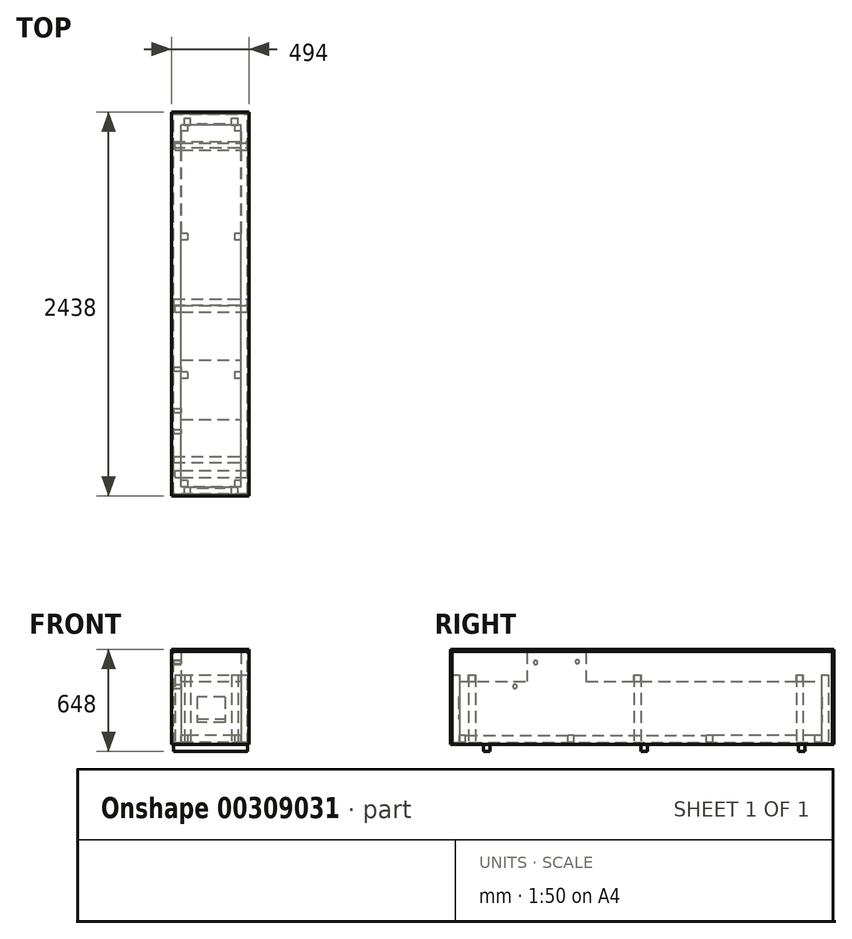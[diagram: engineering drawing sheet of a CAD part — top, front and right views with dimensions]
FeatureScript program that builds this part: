
annotation { "Feature Type Name" : "Feature", "Feature Type Description" : "" }
export const myFeature = defineFeature(function(context is Context, id is Id, definition is map)
    precondition{}
    {
        {
            var Q0;
            Q0=qCreatedBy(makeId("Right.planeOp"),FACE);
            var sketch = newSketch(context, id + "F0", { "sketchPlane" : qUnion([Q0])});
            skLineSegment(sketch, "E0.bottom", {"start": v(-1150, 195) * mm, "end": v(1150, 195) * mm});
            skLineSegment(sketch, "E0.top", {"start": v(-1150, -195) * mm, "end": v(-1110, -195) * mm});
            skLineSegment(sketch, "E0.left", {"start": v(-1150, 195) * mm, "end": v(-1150, -195) * mm});
            skLineSegment(sketch, "E0.right", {"start": v(1150, 195) * mm, "end": v(1150, -195) * mm});
            skPoint(sketch, "E0.middle", {"position": v(0, 0) * mm});
            skLineSegment(sketch, "E1.top", {"start": v(-1110, -148) * mm, "end": v(-460, -148) * mm});
            skLineSegment(sketch, "E1.left", {"start": v(-1110, -195) * mm, "end": v(-1110, -148) * mm});
            skLineSegment(sketch, "E1.right", {"start": v(-460, -195) * mm, "end": v(-460, -148) * mm});
            skLineSegment(sketch, "E2.top", {"start": v(1110, -148) * mm, "end": v(460, -148) * mm});
            skLineSegment(sketch, "E2.left", {"start": v(1110, -195) * mm, "end": v(1110, -148) * mm});
            skLineSegment(sketch, "E2.right", {"start": v(460, -195) * mm, "end": v(460, -148) * mm});
            skLineSegment(sketch, "E3.top", {"start": v(-420, -148) * mm, "end": v(420, -148) * mm});
            skLineSegment(sketch, "E3.left", {"start": v(-420, -195) * mm, "end": v(-420, -148) * mm});
            skLineSegment(sketch, "E3.right", {"start": v(420, -195) * mm, "end": v(420, -148) * mm});
            skLineSegment(sketch, "E4.trimOffspring", {"start": v(-460, -195) * mm, "end": v(-420, -195) * mm});
            skLineSegment(sketch, "E5.trimOffspring", {"start": v(420, -195) * mm, "end": v(460, -195) * mm});
            skLineSegment(sketch, "E6.trimOffspring", {"start": v(1110, -195) * mm, "end": v(1150, -195) * mm});
            skSolve(sketch);
        }
        {
            var Q0;
            Q0 = qSketchRegion(id + "F0", true);
            extrude(context, id + "F1", {"entities" : qUnion([Q0]), "depth" : 380 * mm});
        }
        {
            var Q0;
            Q0=makeQuery(id+"F1.opExtrude","SWEPT_FACE",FACE,{"disambiguationData":[OSD([sQuery(id+"F0.wireOp",EDGE,"E0.left")])]});
            var sketch = newSketch(context, id + "F2", { "sketchPlane" : qUnion([Q0])});
            skLineSegment(sketch, "E7.bottom", {"start": v(40, -195) * mm, "end": v(340, -195) * mm});
            skLineSegment(sketch, "E7.top", {"start": v(40, -148) * mm, "end": v(340, -148) * mm});
            skLineSegment(sketch, "E7.left", {"start": v(40, -195) * mm, "end": v(40, -148) * mm});
            skLineSegment(sketch, "E7.right", {"start": v(340, -195) * mm, "end": v(340, -148) * mm});
            skSolve(sketch);
        }
        {
            var Q0;
            Q0 = qSketchRegion(id + "F2", true);
            extrude(context, id + "F3", {"entities" : qUnion([Q0]), "operationType" : NewBodyOperationType.REMOVE, "endBound" : BoundingType.THROUGH_ALL, "oppositeDirection" : true, "depth" : 25 * mm});
        }
        {
            var Q0;
            Q0=makeQuery(id+"F1.opExtrude","SWEPT_FACE",FACE,{"disambiguationData":[OSD([sQuery(id+"F0.wireOp",EDGE,"E0.bottom")])]});
            var sketch = newSketch(context, id + "F4", { "sketchPlane" : qUnion([Q0])});
            skLineSegment(sketch, "E8.bottom", {"start": v(0, -720) * mm, "end": v(380, -720) * mm});
            skLineSegment(sketch, "E8.top", {"start": v(0, -345) * mm, "end": v(380, -345) * mm});
            skLineSegment(sketch, "E8.left", {"start": v(0, -720) * mm, "end": v(0, -345) * mm});
            skLineSegment(sketch, "E8.right", {"start": v(380, -720) * mm, "end": v(380, -345) * mm});
            skSolve(sketch);
        }
        {
            var Q0;
            Q0 = qSketchRegion(id + "F4", true);
            extrude(context, id + "F5", {"entities" : qUnion([Q0]), "operationType" : NewBodyOperationType.ADD, "depth" : 185 * mm});
        }
        {
            var Q0;
            Q0=makeQuery(id+"F1.opExtrude","SWEPT_FACE",FACE,{"disambiguationData":[OSD([sQuery(id+"F0.wireOp",EDGE,"E0.left")])]});
            var sketch = newSketch(context, id + "F6", { "sketchPlane" : qUnion([Q0])});
            skLineSegment(sketch, "E9.bottom", {"start": v(100, 95) * mm, "end": v(280, 95) * mm});
            skLineSegment(sketch, "E9.top", {"start": v(100, -45) * mm, "end": v(280, -45) * mm});
            skLineSegment(sketch, "E9.left", {"start": v(100, 95) * mm, "end": v(100, -45) * mm});
            skLineSegment(sketch, "E9.right", {"start": v(280, 95) * mm, "end": v(280, -45) * mm});
            skSolve(sketch);
        }
        {
            var Q0;
            Q0 = qSketchRegion(id + "F6", true);
            extrude(context, id + "F7", {"entities" : qUnion([Q0]), "operationType" : NewBodyOperationType.ADD, "depth" : 5 * mm});
        }
        {
            var Q0;
            Q0=makeQuery(id+"F1.opExtrude","SWEPT_FACE",FACE,{"disambiguationData":[OSD([sQuery(id+"F0.wireOp",EDGE,"E0.right")])]});
            var sketch = newSketch(context, id + "F8", { "sketchPlane" : qUnion([Q0])});
            skLineSegment(sketch, "E10.bottom", {"start": v(-280, 95) * mm, "end": v(-100, 95) * mm});
            skLineSegment(sketch, "E10.top", {"start": v(-280, -65) * mm, "end": v(-100, -65) * mm});
            skLineSegment(sketch, "E10.left", {"start": v(-280, 95) * mm, "end": v(-280, -65) * mm});
            skLineSegment(sketch, "E10.right", {"start": v(-100, 95) * mm, "end": v(-100, -65) * mm});
            skSolve(sketch);
        }
        {
            var Q0;
            Q0 = qSketchRegion(id + "F8", true);
            extrude(context, id + "F9", {"entities" : qUnion([Q0]), "operationType" : NewBodyOperationType.ADD, "depth" : 5 * mm});
        }
        {
            var Q0;
            Q0=makeQuery(id+"F5.boolean.opBoolean","MERGE",FACE,{"derivedFrom":[makeQuery(id+"F1.opExtrude","CAP_FACE",FACE,{"disambiguationData":[OSD([sQuery(id+"F0.wireOp",EDGE,"E0.bottom"),sQuery(id+"F0.wireOp",EDGE,"E0.top"),sQuery(id+"F0.wireOp",EDGE,"E0.left"),sQuery(id+"F0.wireOp",EDGE,"E0.right"),sQuery(id+"F0.wireOp",EDGE,"E1.top"),sQuery(id+"F0.wireOp",EDGE,"E1.left"),sQuery(id+"F0.wireOp",EDGE,"E1.right"),sQuery(id+"F0.wireOp",EDGE,"E2.top"),sQuery(id+"F0.wireOp",EDGE,"E2.left"),sQuery(id+"F0.wireOp",EDGE,"E2.right"),sQuery(id+"F0.wireOp",EDGE,"E3.top"),sQuery(id+"F0.wireOp",EDGE,"E3.left"),sQuery(id+"F0.wireOp",EDGE,"E3.right"),sQuery(id+"F0.wireOp",EDGE,"E4.trimOffspring"),sQuery(id+"F0.wireOp",EDGE,"E5.trimOffspring"),sQuery(id+"F0.wireOp",EDGE,"E6.trimOffspring")])],"isStart":true}),makeQuery(id+"F5.opExtrude","SWEPT_FACE",FACE,{"disambiguationData":[OSD([sQuery(id+"F4.wireOp",EDGE,"E8.left")])]})]});
            var sketch = newSketch(context, id + "F10", { "sketchPlane" : qUnion([Q0])});
            skCircle(sketch, "E11", {"center": v(399.4, 319.26) * mm, "radius": 12.5 * mm});
            skCircle(sketch, "E12", {"center": v(664.97, 313.36) * mm, "radius": 12.5 * mm});
            skCircle(sketch, "E13", {"center": v(796.28, 162.13) * mm, "radius": 12.5 * mm});
            skSolve(sketch);
        }
        {
            var Q0;
            Q0 = qSketchRegion(id + "F10", true);
            extrude(context, id + "F11", {"entities" : qUnion([Q0]), "operationType" : NewBodyOperationType.ADD, "depth" : 50 * mm});
        }
        {
            var Q0;
            {var subQ2=sQuery(id+"F0.wireOp",EDGE,"E0.top");Q0=makeQuery(id+"F3.boolean.opBoolean","SPLIT",FACE,{"disambiguationData":[TD([makeQuery(id+"F3.opExtrude","SWEPT_FACE",FACE,{"disambiguationData":[OSD([sQuery(id+"F2.wireOp",EDGE,"E7.right")])]})])],"derivedFrom":makeQuery(id+"F1.opExtrude","SWEPT_FACE",FACE,{"disambiguationData":[OSD([subQ2])]})});}
            var sketch = newSketch(context, id + "F12", { "sketchPlane" : qUnion([Q0])});
            skLineSegment(sketch, "E14.bottom", {"start": v(420, 1195) * mm, "end": v(-50, 1195) * mm});
            skLineSegment(sketch, "E14.top", {"start": v(420, -1219) * mm, "end": v(-50, -1219) * mm});
            skLineSegment(sketch, "E14.left", {"start": v(420, 1195) * mm, "end": v(420, -1219) * mm});
            skLineSegment(sketch, "E14.right", {"start": v(-50, 1195) * mm, "end": v(-50, -1219) * mm});
            skSolve(sketch);
        }
        {
            var Q0;
            Q0 = qSketchRegion(id + "F12", true);
            extrude(context, id + "F13", {"entities" : qUnion([Q0]), "depth" : 12 * mm});
        }
        {
            var Q0;
            Q0=makeQuery(id+"F13.opExtrude","SWEPT_FACE",FACE,{"disambiguationData":[OSD([sQuery(id+"F12.wireOp",EDGE,"E14.left")])]});
            var sketch = newSketch(context, id + "F14", { "sketchPlane" : qUnion([Q0])});
            skLineSegment(sketch, "E15.top", {"start": v(-1195, 385) * mm, "end": v(1219, 385) * mm});
            skLineSegment(sketch, "E15.left", {"start": v(-1195, -195) * mm, "end": v(-1195, 385) * mm});
            skLineSegment(sketch, "E15.right", {"start": v(1219, -195) * mm, "end": v(1219, 385) * mm});
            skLineSegment(sketch, "E16.top", {"start": v(-1195, -207) * mm, "end": v(1219, -207) * mm});
            skLineSegment(sketch, "E16.left", {"start": v(-1195, -195) * mm, "end": v(-1195, -207) * mm});
            skLineSegment(sketch, "E16.right", {"start": v(1219, -195) * mm, "end": v(1219, -207) * mm});
            skSolve(sketch);
        }
        {
            var Q0;
            Q0 = qSketchRegion(id + "F14", true);
            extrude(context, id + "F15", {"entities" : qUnion([Q0]), "depth" : 12 * mm});
        }
        {
            var Q0;
            Q0=makeQuery(id+"F15.opExtrude","SWEPT_BODY",BODY,{"disambiguationData":[OSD([sQuery(id+"F14.wireOp",EDGE,"E15.bottom"),sQuery(id+"F14.wireOp",EDGE,"E15.top"),sQuery(id+"F14.wireOp",EDGE,"E15.left"),sQuery(id+"F14.wireOp",EDGE,"E15.right")])]});
            transform(context, id + "F16", {"entities" : qUnion([Q0]), "transformType" : TransformType.TRANSLATION_3D, "dx" : -482 * mm, "dy" : 0 * mm, "dz" : 0 * mm, "makeCopy" : true});
        }
        {
            var Q0;
            Q0=makeQuery(id+"F13.opExtrude","CAP_FACE",FACE,{"disambiguationData":[OSD([sQuery(id+"F12.wireOp",EDGE,"E14.bottom"),sQuery(id+"F12.wireOp",EDGE,"E14.top"),sQuery(id+"F12.wireOp",EDGE,"E14.left"),sQuery(id+"F12.wireOp",EDGE,"E14.right")])],"isStart":true});
            var sketch = newSketch(context, id + "F17", { "sketchPlane" : qUnion([Q0])});
            skLineSegment(sketch, "E17.bottom", {"start": v(380, -1090) * mm, "end": v(420, -1090) * mm});
            skLineSegment(sketch, "E17.top", {"start": v(380, -1046) * mm, "end": v(420, -1046) * mm});
            skLineSegment(sketch, "E17.left", {"start": v(380, -1090) * mm, "end": v(380, -1046) * mm});
            skLineSegment(sketch, "E17.right", {"start": v(420, -1090) * mm, "end": v(420, -1046) * mm});
            skSolve(sketch);
        }
        {
            var Q0;
            Q0 = qSketchRegion(id + "F17", true);
            extrude(context, id + "F18", {"entities" : qUnion([Q0]), "depth" : 430 * mm});
        }
        {
            var Q0;
            Q0=makeQuery(id+"F13.opExtrude","SWEPT_FACE",FACE,{"disambiguationData":[OSD([sQuery(id+"F12.wireOp",EDGE,"E14.left")])]});
            var sketch = newSketch(context, id + "F19", { "sketchPlane" : qUnion([Q0])});
            skLineSegment(sketch, "E18.bottom", {"start": v(-995, -207) * mm, "end": v(-955, -207) * mm});
            skLineSegment(sketch, "E18.top", {"start": v(-995, -251) * mm, "end": v(-955, -251) * mm});
            skLineSegment(sketch, "E18.left", {"start": v(-995, -207) * mm, "end": v(-995, -251) * mm});
            skLineSegment(sketch, "E18.right", {"start": v(-955, -207) * mm, "end": v(-955, -251) * mm});
            skLineSegment(sketch, "E19.1.0.0", {"start": v(5, -207) * mm, "end": v(5, -251) * mm});
            skLineSegment(sketch, "E19.1.0.1", {"start": v(45, -207) * mm, "end": v(45, -251) * mm});
            skLineSegment(sketch, "E19.1.0.2", {"start": v(5, -207) * mm, "end": v(45, -207) * mm});
            skLineSegment(sketch, "E19.1.0.3", {"start": v(5, -251) * mm, "end": v(45, -251) * mm});
            skLineSegment(sketch, "E19.2.0.0", {"start": v(1005, -207) * mm, "end": v(1005, -251) * mm});
            skLineSegment(sketch, "E19.2.0.1", {"start": v(1045, -207) * mm, "end": v(1045, -251) * mm});
            skLineSegment(sketch, "E19.2.0.2", {"start": v(1005, -207) * mm, "end": v(1045, -207) * mm});
            skLineSegment(sketch, "E19.2.0.3", {"start": v(1005, -251) * mm, "end": v(1045, -251) * mm});
            skLineSegment(sketch, "E19.direction1", {"start": v(-995, -251) * mm, "end": v(5, -251) * mm, "construction": true});
            skSolve(sketch);
        }
        {
            var Q0;
            Q0 = qSketchRegion(id + "F19", true);
            var Q1;
            Q1=makeQuery(id+"F16.opPattern","COPY",FACE,{"derivedFrom":makeQuery(id+"F15.opExtrude","CAP_FACE",FACE,{"disambiguationData":[OSD([sQuery(id+"F14.wireOp",EDGE,"E15.bottom"),sQuery(id+"F14.wireOp",EDGE,"E15.top"),sQuery(id+"F14.wireOp",EDGE,"E15.left"),sQuery(id+"F14.wireOp",EDGE,"E15.right")])],"isStart":false}),"instanceName":"1"});
            extrude(context, id + "F20", {"entities" : qUnion([Q0]), "endBound" : BoundingType.UP_TO_SURFACE, "oppositeDirection" : true, "endBoundEntityFace" : qUnion([Q1]), "depth" : 25 * mm});
        }
        {
            var Q0;
            Q0=makeQuery(id+"F18.opExtrude","SWEPT_BODY",BODY,{"disambiguationData":[OSD([sQuery(id+"F17.wireOp",EDGE,"E17.bottom"),sQuery(id+"F17.wireOp",EDGE,"E17.top"),sQuery(id+"F17.wireOp",EDGE,"E17.left"),sQuery(id+"F17.wireOp",EDGE,"E17.right")])]});
            transform(context, id + "F21", {"entities" : qUnion([Q0]), "transformType" : TransformType.TRANSLATION_3D, "dx" : -420 * mm, "dy" : 0 * mm, "dz" : 0 * mm, "makeCopy" : true});
        }
        {
            var Q0;
            Q0=makeQuery(id+"F21.opPattern","COPY",FACE,{"derivedFrom":makeQuery(id+"F18.opExtrude","CAP_FACE",FACE,{"disambiguationData":[OSD([sQuery(id+"F17.wireOp",EDGE,"E17.bottom"),sQuery(id+"F17.wireOp",EDGE,"E17.top"),sQuery(id+"F17.wireOp",EDGE,"E17.left"),sQuery(id+"F17.wireOp",EDGE,"E17.right")])],"isStart":false}),"instanceName":"1"});
            var sketch = newSketch(context, id + "F22", { "sketchPlane" : qUnion([Q0])});
            skLineSegment(sketch, "E20.bottom", {"start": v(0, -1090) * mm, "end": v(380, -1090) * mm});
            skLineSegment(sketch, "E20.top", {"start": v(0, -1046) * mm, "end": v(380, -1046) * mm});
            skLineSegment(sketch, "E20.left", {"start": v(0, -1090) * mm, "end": v(0, -1046) * mm});
            skLineSegment(sketch, "E20.right", {"start": v(380, -1090) * mm, "end": v(380, -1046) * mm});
            skSolve(sketch);
        }
        {
            var Q0;
            Q0 = qSketchRegion(id + "F22", true);
            extrude(context, id + "F23", {"entities" : qUnion([Q0]), "oppositeDirection" : true, "depth" : 40 * mm});
        }
        {
            var Q0;
            Q0=makeQuery(id+"F23.opExtrude","SWEPT_BODY",BODY,{"disambiguationData":[OSD([sQuery(id+"F22.wireOp",EDGE,"E20.bottom"),sQuery(id+"F22.wireOp",EDGE,"E20.top"),sQuery(id+"F22.wireOp",EDGE,"E20.left"),sQuery(id+"F22.wireOp",EDGE,"E20.right")])]});
            var Q1;
            Q1=makeQuery(id+"F21.opPattern","COPY",BODY,{"derivedFrom":makeQuery(id+"F18.opExtrude","SWEPT_BODY",BODY,{"disambiguationData":[OSD([sQuery(id+"F17.wireOp",EDGE,"E17.bottom"),sQuery(id+"F17.wireOp",EDGE,"E17.top"),sQuery(id+"F17.wireOp",EDGE,"E17.left"),sQuery(id+"F17.wireOp",EDGE,"E17.right")])]}),"instanceName":"1"});
            var Q2;
            Q2=makeQuery(id+"F18.opExtrude","SWEPT_BODY",BODY,{"disambiguationData":[OSD([sQuery(id+"F17.wireOp",EDGE,"E17.bottom"),sQuery(id+"F17.wireOp",EDGE,"E17.top"),sQuery(id+"F17.wireOp",EDGE,"E17.left"),sQuery(id+"F17.wireOp",EDGE,"E17.right")])]});
            transform(context, id + "F24", {"entities" : qUnion([Q0, Q1, Q2]), "transformType" : TransformType.TRANSLATION_3D, "dx" : 0 * mm, "dy" : 1050 * mm, "dz" : 0 * mm, "makeCopy" : true});
        }
        {
            var Q0;
            Q0=makeQuery(id+"F23.opExtrude","SWEPT_BODY",BODY,{"disambiguationData":[OSD([sQuery(id+"F22.wireOp",EDGE,"E20.bottom"),sQuery(id+"F22.wireOp",EDGE,"E20.top"),sQuery(id+"F22.wireOp",EDGE,"E20.left"),sQuery(id+"F22.wireOp",EDGE,"E20.right")])]});
            var Q1;
            Q1=makeQuery(id+"F21.opPattern","COPY",BODY,{"derivedFrom":makeQuery(id+"F18.opExtrude","SWEPT_BODY",BODY,{"disambiguationData":[OSD([sQuery(id+"F17.wireOp",EDGE,"E17.bottom"),sQuery(id+"F17.wireOp",EDGE,"E17.top"),sQuery(id+"F17.wireOp",EDGE,"E17.left"),sQuery(id+"F17.wireOp",EDGE,"E17.right")])]}),"instanceName":"1"});
            var Q2;
            Q2=makeQuery(id+"F18.opExtrude","SWEPT_BODY",BODY,{"disambiguationData":[OSD([sQuery(id+"F17.wireOp",EDGE,"E17.bottom"),sQuery(id+"F17.wireOp",EDGE,"E17.top"),sQuery(id+"F17.wireOp",EDGE,"E17.left"),sQuery(id+"F17.wireOp",EDGE,"E17.right")])]});
            transform(context, id + "F25", {"entities" : qUnion([Q0, Q1, Q2]), "transformType" : TransformType.TRANSLATION_3D, "dx" : 0 * mm, "dy" : 2080 * mm, "dz" : 0 * mm, "makeCopy" : true});
        }
        {
            var Q0;
            Q0=makeQuery(id+"F18.opExtrude","SWEPT_BODY",BODY,{"disambiguationData":[OSD([sQuery(id+"F17.wireOp",EDGE,"E17.bottom"),sQuery(id+"F17.wireOp",EDGE,"E17.top"),sQuery(id+"F17.wireOp",EDGE,"E17.left"),sQuery(id+"F17.wireOp",EDGE,"E17.right")])]});
            transform(context, id + "F26", {"entities" : qUnion([Q0]), "transformType" : TransformType.TRANSLATION_3D, "dx" : -60 * mm, "dy" : -104 * mm, "dz" : 0 * mm, "makeCopy" : true});
        }
        {
            var Q0;
            Q0=makeQuery(id+"F21.opPattern","COPY",BODY,{"derivedFrom":makeQuery(id+"F18.opExtrude","SWEPT_BODY",BODY,{"disambiguationData":[OSD([sQuery(id+"F17.wireOp",EDGE,"E17.bottom"),sQuery(id+"F17.wireOp",EDGE,"E17.top"),sQuery(id+"F17.wireOp",EDGE,"E17.left"),sQuery(id+"F17.wireOp",EDGE,"E17.right")])]}),"instanceName":"1"});
            transform(context, id + "F27", {"entities" : qUnion([Q0]), "transformType" : TransformType.TRANSLATION_3D, "dx" : 60 * mm, "dy" : -104 * mm, "dz" : 0 * mm, "makeCopy" : true});
        }
        {
            var Q0;
            Q0=makeQuery(id+"F27.opPattern","COPY",BODY,{"derivedFrom":makeQuery(id+"F21.opPattern","COPY",BODY,{"derivedFrom":makeQuery(id+"F18.opExtrude","SWEPT_BODY",BODY,{"disambiguationData":[OSD([sQuery(id+"F17.wireOp",EDGE,"E17.bottom"),sQuery(id+"F17.wireOp",EDGE,"E17.top"),sQuery(id+"F17.wireOp",EDGE,"E17.left"),sQuery(id+"F17.wireOp",EDGE,"E17.right")])]}),"instanceName":"1"}),"instanceName":"1"});
            var Q1;
            Q1=makeQuery(id+"F26.opPattern","COPY",BODY,{"derivedFrom":makeQuery(id+"F18.opExtrude","SWEPT_BODY",BODY,{"disambiguationData":[OSD([sQuery(id+"F17.wireOp",EDGE,"E17.bottom"),sQuery(id+"F17.wireOp",EDGE,"E17.top"),sQuery(id+"F17.wireOp",EDGE,"E17.left"),sQuery(id+"F17.wireOp",EDGE,"E17.right")])]}),"instanceName":"1"});
            transform(context, id + "F28", {"entities" : qUnion([Q0, Q1]), "transformType" : TransformType.TRANSLATION_3D, "dx" : 0 * mm, "dy" : 2344 * mm, "dz" : 0 * mm, "makeCopy" : true});
        }
        {
            var Q0;
            Q0=makeQuery(id+"F16.opPattern","COPY",FACE,{"derivedFrom":makeQuery(id+"F15.opExtrude","SWEPT_FACE",FACE,{"disambiguationData":[OSD([sQuery(id+"F14.wireOp",EDGE,"E15.left"),sQuery(id+"F14.wireOp",EDGE,"E16.left")])]}),"instanceName":"1"});
            var sketch = newSketch(context, id + "F29", { "sketchPlane" : qUnion([Q0])});
            skLineSegment(sketch, "E21.bottom", {"start": v(-62, -207) * mm, "end": v(432, -207) * mm});
            skLineSegment(sketch, "E21.top", {"start": v(-62, 385) * mm, "end": v(432, 385) * mm});
            skLineSegment(sketch, "E21.left", {"start": v(-62, -207) * mm, "end": v(-62, 385) * mm});
            skLineSegment(sketch, "E21.right", {"start": v(432, -207) * mm, "end": v(432, 385) * mm});
            skSolve(sketch);
        }
        {
            var Q0;
            Q0 = qSketchRegion(id + "F29", true);
            extrude(context, id + "F30", {"entities" : qUnion([Q0]), "depth" : 12 * mm});
        }
        {
            var Q0;
            Q0=makeQuery(id+"F30.opExtrude","SWEPT_BODY",BODY,{"disambiguationData":[OSD([sQuery(id+"F29.wireOp",EDGE,"E21.bottom"),sQuery(id+"F29.wireOp",EDGE,"E21.top"),sQuery(id+"F29.wireOp",EDGE,"E21.left"),sQuery(id+"F29.wireOp",EDGE,"E21.right")])]});
            transform(context, id + "F31", {"entities" : qUnion([Q0]), "transformType" : TransformType.TRANSLATION_3D, "dx" : 0 * mm, "dy" : 2426 * mm, "dz" : 0 * mm, "makeCopy" : true});
        }
        {
            var Q0;
            Q0=makeQuery(id+"F16.opPattern","COPY",FACE,{"derivedFrom":makeQuery(id+"F15.opExtrude","SWEPT_FACE",FACE,{"disambiguationData":[OSD([sQuery(id+"F14.wireOp",EDGE,"E15.top")])]}),"instanceName":"1"});
            var sketch = newSketch(context, id + "F32", { "sketchPlane" : qUnion([Q0])});
            skLineSegment(sketch, "E22.bottom", {"start": v(-62, -1207) * mm, "end": v(432, -1207) * mm});
            skLineSegment(sketch, "E22.top", {"start": v(-62, 1231) * mm, "end": v(432, 1231) * mm});
            skLineSegment(sketch, "E22.left", {"start": v(-62, -1207) * mm, "end": v(-62, 1231) * mm});
            skLineSegment(sketch, "E22.right", {"start": v(432, -1207) * mm, "end": v(432, 1231) * mm});
            skSolve(sketch);
        }
        {
            var Q0;
            Q0 = qSketchRegion(id + "F32", true);
            extrude(context, id + "F33", {"entities" : qUnion([Q0]), "depth" : 12 * mm});
        }
    });
